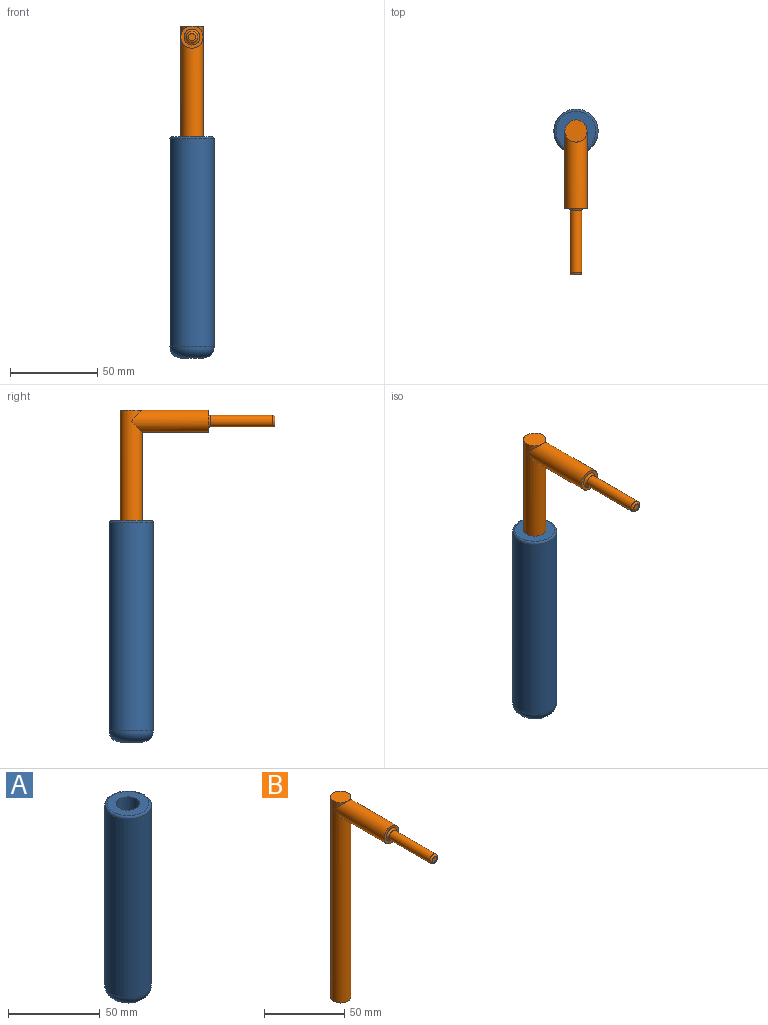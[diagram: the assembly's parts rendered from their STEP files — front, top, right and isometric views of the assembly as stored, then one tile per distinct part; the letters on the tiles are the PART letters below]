
ASSEMBLY  parts=2 mates=1
PART A: 7 faces, bbox 27.5x27.5x127 mm
  f0: cylinder r=12.7mm len=119.38mm, axis (0,0,-1), area 9526.1mm2, adj f5,f6
  f1: plane 22.86x22.86mm, normal (0,0,1), area 286.3mm2, adj f3,f6
  f2: plane 12.7x12.7mm, normal (0,0,-1), area 126.7mm2, adj f5
  f3: cylinder r=6.29mm len=88.9mm, axis (0,0,1), area 3511.5mm2, adj f1,f4
  f4: plane 12.57x12.57mm, normal (0,0,1), area 124.2mm2, adj f3
  f5: torus R=6.35mm, axis (0,0,1), area 651.3mm2, adj f0,f2
  f6: torus R=11.43mm, axis (0,0,1), area 153.4mm2, adj f0,f1
PART B: 10 faces, bbox 12.7x88.9x152.4 mm
  f0: cylinder r=6.35mm len=152.4mm, axis (0,0,-1), area 5896.2mm2, adj f1,f2,f3,f4
  f1: cylinder r=6.35mm len=6.35mm, axis (0,0,-1), area 23mm2, adj f0,f2,f4
  f2: plane 12.7x12.7mm, normal (0,0,1), area 126.7mm2, adj f0,f1
  f3: plane 12.7x12.7mm, normal (0,0,-1), area 126.7mm2, adj f0
  f4: cylinder r=6.35mm len=44.45mm, axis (0,1,0), area 1612.2mm2, adj f0,f1,f5
  f5: plane 12.7x12.7mm, normal (0,-1,0), area 61mm2, adj f4,f8
  f6: cylinder r=3.3mm len=35.56mm, axis (0,1,0), area 737.8mm2, adj f8,f9
  f7: plane 4.06x4.06mm, normal (0,-1,0), area 13mm2, adj f9
  f8: torus R=4.57mm, axis (0,-1,0), area 47.2mm2, adj f5,f6
  f9: torus R=2.03mm, axis (0,-1,0), area 35.6mm2, adj f6,f7
PLACE A at identity
PLACE B t=(0,0,38.1)mm
MATE cylindrical B.f0 <-> A.f3  axis (0,0,-1) through (0,0,38.1)mm
